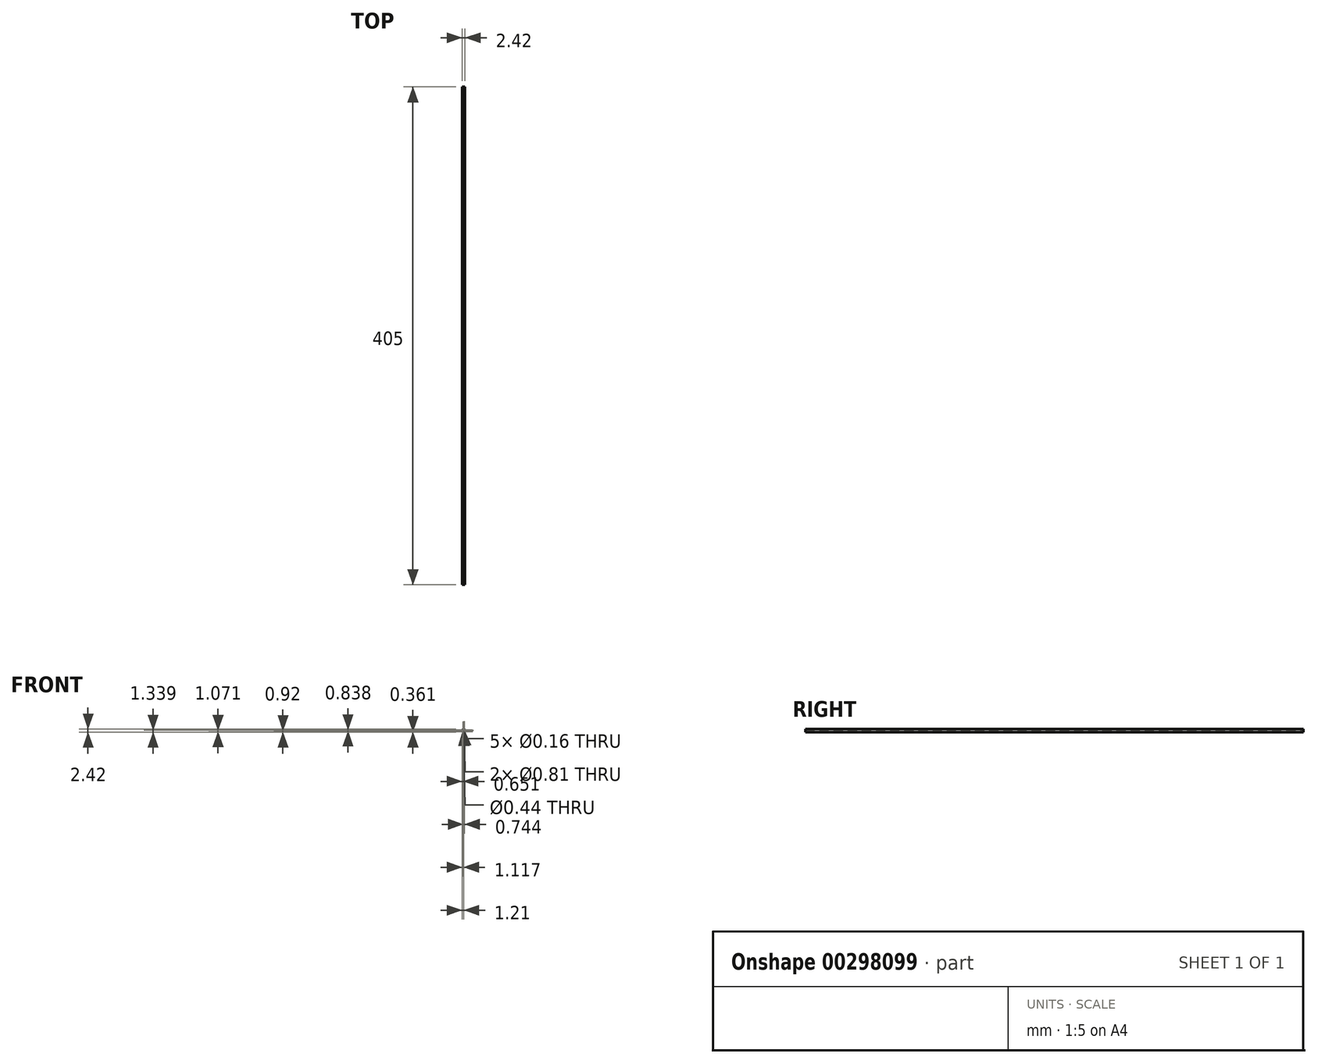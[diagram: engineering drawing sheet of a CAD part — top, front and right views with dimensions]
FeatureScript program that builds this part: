
annotation { "Feature Type Name" : "Feature", "Feature Type Description" : "" }
export const myFeature = defineFeature(function(context is Context, id is Id, definition is map)
    precondition{}
    {
        {
            var Q0;
            Q0=qCreatedBy(makeId("Front.planeOp"),FACE);
            var sketch = newSketch(context, id + "F0", { "sketchPlane" : qUnion([Q0])});
            skCircle(sketch, "E0", {"center": v(0, 0) * mm, "radius": 0.4 * mm});
            skCircle(sketch, "E1", {"center": v(-0.1, -0.56) * mm, "radius": 0.08 * mm});
            skCircle(sketch, "E2", {"center": v(0.1, -0.56) * mm, "radius": 0.08 * mm});
            skCircle(sketch, "E3", {"center": v(0, 0.84) * mm, "radius": 0.4 * mm});
            skCircle(sketch, "E4", {"center": v(0.65, 0.51) * mm, "radius": 0.08 * mm});
            skCircle(sketch, "E5", {"center": v(0.65, 0.32) * mm, "radius": 0.08 * mm});
            skCircle(sketch, "E6", {"center": v(0.47, 0.42) * mm, "radius": 0.08 * mm});
            skCircle(sketch, "E7", {"center": v(0.56, 0.42) * mm, "radius": 0.22 * mm});
            skEllipse(sketch, "E8", {"center": v(0, -0.56) * mm, "majorRadius": 0.23 * mm, "minorRadius": 0.11 * mm, "majorAxis": v(1, 0)});
            skCircle(sketch, "E9.MirrorC", {"center": v(-0.56, 0.42) * mm, "radius": 0.22 * mm});
            skCircle(sketch, "E10.MirrorC", {"center": v(-0.65, 0.51) * mm, "radius": 0.08 * mm});
            skCircle(sketch, "E11.MirrorC", {"center": v(-0.47, 0.42) * mm, "radius": 0.08 * mm});
            skCircle(sketch, "E12.MirrorC", {"center": v(-0.65, 0.32) * mm, "radius": 0.08 * mm});
            skPoint(sketch, "E13", {"position": v(0, 1.24) * mm});
            skPoint(sketch, "E14", {"position": v(0, -0.67) * mm});
            skPoint(sketch, "E15", {"position": v(0, 0.29) * mm});
            skCircle(sketch, "E16", {"center": v(0, 0.29) * mm, "radius": 1.2 * mm});
            skCircle(sketch, "E17", {"center": v(0, 0.29) * mm, "radius": 1.05 * mm});
            skSolve(sketch);
        }
        {
            var Q0;
            Q0=qSketchRegion(id+"F0",true);
            var Q1;
            Q1=makeQuery(id+"F0.imprint","IMPRINT",FACE,{"disambiguationData":[TD([[makeQuery(id+"F0.imprint","IMPRINT",EDGE,{"derivedFrom":sQuery(id+"F0.wireOp",EDGE,"E0")}),-1.0]])]});
            var Q2;
            Q2=makeQuery(id+"F0.imprint","IMPRINT",FACE,{"disambiguationData":[TD([[makeQuery(id+"F0.imprint","IMPRINT",EDGE,{"derivedFrom":sQuery(id+"F0.wireOp",EDGE,"E9.MirrorC")}),-1.0]])]});
            var Q3;
            Q3=makeQuery(id+"F0.imprint","IMPRINT",FACE,{"disambiguationData":[TD([[makeQuery(id+"F0.imprint","IMPRINT",EDGE,{"derivedFrom":sQuery(id+"F0.wireOp",EDGE,"E4")}),-1.0]])]});
            var Q4;
            Q4=makeQuery(id+"F0.imprint","IMPRINT",FACE,{"disambiguationData":[TD([[makeQuery(id+"F0.imprint","IMPRINT",EDGE,{"derivedFrom":sQuery(id+"F0.wireOp",EDGE,"E16")}),1.0]])]});
            var Q5;
            Q5=makeQuery(id+"F0.imprint","IMPRINT",FACE,{"disambiguationData":[TD([[makeQuery(id+"F0.imprint","IMPRINT",EDGE,{"derivedFrom":sQuery(id+"F0.wireOp",EDGE,"E1")}),-1.0]])]});
            extrude(context, id + "F1", {"entities" : qUnion([Q0, Q1, Q2, Q3, Q4, Q5]), "depth" : 405 * mm});
        }
    });
